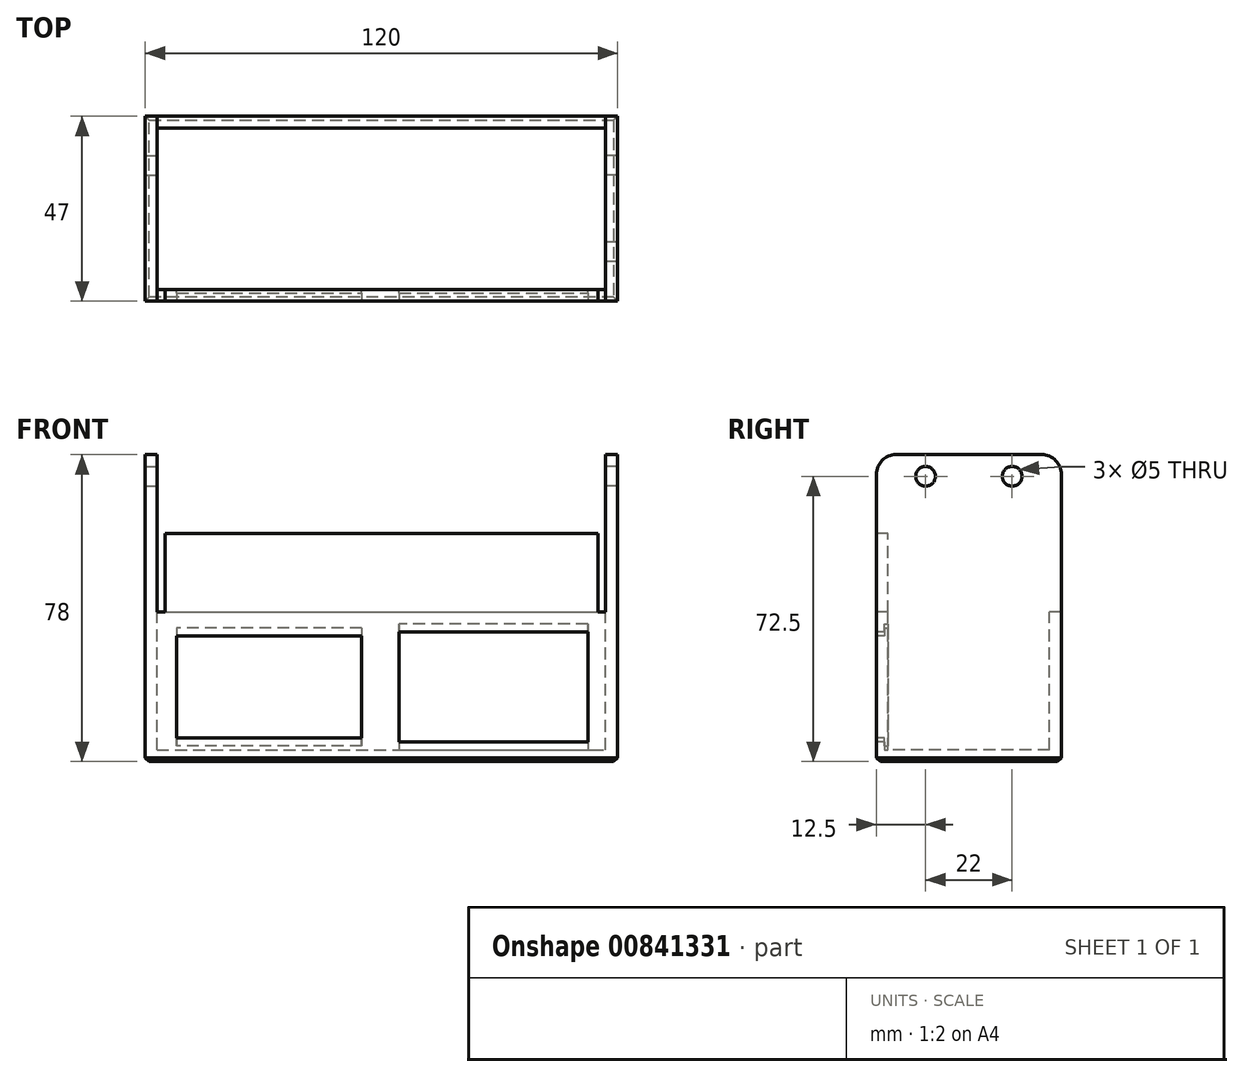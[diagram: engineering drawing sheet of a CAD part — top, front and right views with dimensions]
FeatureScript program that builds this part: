
annotation { "Feature Type Name" : "Feature", "Feature Type Description" : "" }
export const myFeature = defineFeature(function(context is Context, id is Id, definition is map)
    precondition{}
    {
        {
            assignVariable(context, id + "F0", {"name" : "wall", "anyValue" : 3});
        }
        {
            assignVariable(context, id + "F1", {"name" : "width", "anyValue" : 114});
        }
        {
            var Q0;
            Q0=qCreatedBy(makeId("Right.planeOp"),FACE);
            var sketch = newSketch(context, id + "F2", { "sketchPlane" : qUnion([Q0])});
            skLineSegment(sketch, "E0.bottom", {"start": v(17.5, 40) * mm, "end": v(-19.5, 40) * mm});
            skLineSegment(sketch, "E0.top", {"start": v(22.5, -38) * mm, "end": v(-24.5, -38) * mm});
            skLineSegment(sketch, "E0.left", {"start": v(22.5, 35) * mm, "end": v(22.5, -38) * mm});
            skLineSegment(sketch, "E0.right", {"start": v(-24.5, 35) * mm, "end": v(-24.5, -38) * mm});
            skCircle(sketch, "E1", {"center": v(10, 34.5) * mm, "radius": 2.5 * mm});
            skCircle(sketch, "E2", {"center": v(-12, 34.5) * mm, "radius": 2.5 * mm});
            skPoint(sketch, "E3.visualSharp", {"position": v(-24.5, 40) * mm});
            skArc(sketch, "E3.filletArc", {"start": v(-19.5, 40) * mm, "mid": v(-23.04, 38.54) * mm, "end": v(-24.5, 35) * mm});
            skPoint(sketch, "E4.visualSharp", {"position": v(22.5, 40) * mm});
            skArc(sketch, "E4.filletArc", {"start": v(22.5, 35) * mm, "mid": v(21.04, 38.54) * mm, "end": v(17.5, 40) * mm});
            skSolve(sketch);
        }
        {
            var Q0;
            Q0=qSketchRegion(id+"F2",true);
            extrude(context, id + "F3", {"entities" : qUnion([Q0]), "depth" : (getVariable(context, 'wall')) * mm, "offsetDistance" : 25 * mm});
        }
        {
            var Q0;
            Q0=qCreatedBy(makeId("Right.planeOp"),FACE);
            var sketch = newSketch(context, id + "F4", { "sketchPlane" : qUnion([Q0])});
            skLineSegment(sketch, "E5.bottom", {"start": v(22.5, -38) * mm, "end": v(-24.5, -38) * mm});
            skLineSegment(sketch, "E5.top", {"start": v(22.5, -35) * mm, "end": v(-24.5, -35) * mm});
            skLineSegment(sketch, "E5.left", {"start": v(22.5, -38) * mm, "end": v(22.5, -35) * mm});
            skLineSegment(sketch, "E5.right", {"start": v(-24.5, -38) * mm, "end": v(-24.5, -35) * mm});
            skLineSegment(sketch, "E6.bottom", {"start": v(-24.5, -38) * mm, "end": v(-21.5, -38) * mm});
            skLineSegment(sketch, "E6.top", {"start": v(-24.5, 0) * mm, "end": v(-21.5, 0) * mm});
            skLineSegment(sketch, "E6.left", {"start": v(-24.5, -38) * mm, "end": v(-24.5, 0) * mm});
            skLineSegment(sketch, "E6.right", {"start": v(-21.5, -38) * mm, "end": v(-21.5, 0) * mm});
            skLineSegment(sketch, "E7.bottom", {"start": v(22.5, -38) * mm, "end": v(19.5, -38) * mm});
            skLineSegment(sketch, "E7.top", {"start": v(22.5, 0) * mm, "end": v(19.5, 0) * mm});
            skLineSegment(sketch, "E7.left", {"start": v(22.5, -38) * mm, "end": v(22.5, 0) * mm});
            skLineSegment(sketch, "E7.right", {"start": v(19.5, -38) * mm, "end": v(19.5, 0) * mm});
            skSolve(sketch);
        }
        {
            var Q0;
            {var subQ0=sQuery(id+"F4.wireOp",EDGE,"E5.right");var subQ1=sQuery(id+"F4.wireOp",EDGE,"E5.bottom");var subQ9=sQuery(id+"F4.wireOp",EDGE,"E7.right");var subQ10=makeQuery(id+"F4.imprint","INTERSECT",VERTEX,{"derivedFrom":[subQ1,subQ9]});var subQ14=sQuery(id+"F4.wireOp",EDGE,"E5.left");var subQ16=sQuery(id+"F4.wireOp",EDGE,"E7.top");var subQ17=sQuery(id+"F4.wireOp",EDGE,"E6.top");Q0=qUnion([makeQuery(id+"F4.imprint","IMPRINT",FACE,{"disambiguationData":[TD([[makeQuery(id+"F4.imprint","IMPRINT",EDGE,{"derivedFrom":subQ17}),-1.0]])]}),makeQuery(id+"F4.imprint","IMPRINT",FACE,{"disambiguationData":[TD([[makeQuery(id+"F4.imprint","IMPRINT",EDGE,{"derivedFrom":subQ14}),1.0]])]}),makeQuery(id+"F4.imprint","IMPRINT",FACE,{"disambiguationData":[TD([[makeQuery(id+"F4.imprint","IMPRINT",EDGE,{"derivedFrom":subQ16}),1.0]])]}),makeQuery(id+"F4.imprint","IMPRINT",FACE,{"disambiguationData":[TD([[makeQuery(id+"F4.imprint","IMPRINT",EDGE,{"disambiguationData":[TD([[subQ10,-1.0]])],"derivedFrom":subQ1}),-1.0]])]}),makeQuery(id+"F4.imprint","IMPRINT",FACE,{"disambiguationData":[TD([[makeQuery(id+"F4.imprint","IMPRINT",EDGE,{"derivedFrom":subQ0}),-1.0]])]})]);}
            extrude(context, id + "F5", {"entities" : qUnion([Q0]), "operationType" : NewBodyOperationType.ADD, "oppositeDirection" : true, "depth" : (getVariable(context, 'width')) * mm, "offsetDistance" : 25 * mm});
        }
        {
            var Q0;
            Q0=makeQuery(id+"F5.opExtrude","CAP_FACE",FACE,{"disambiguationData":[OSD([sQuery(id+"F4.wireOp",EDGE,"E5.bottom"),sQuery(id+"F4.wireOp",EDGE,"E5.top"),sQuery(id+"F4.wireOp",EDGE,"E5.left"),sQuery(id+"F4.wireOp",EDGE,"E5.right"),sQuery(id+"F4.wireOp",EDGE,"E6.top"),sQuery(id+"F4.wireOp",EDGE,"E6.left"),sQuery(id+"F4.wireOp",EDGE,"E6.right"),sQuery(id+"F4.wireOp",EDGE,"E7.top"),sQuery(id+"F4.wireOp",EDGE,"E7.left"),sQuery(id+"F4.wireOp",EDGE,"E7.right")])],"isStart":false});
            var sketch = newSketch(context, id + "F6", { "sketchPlane" : qUnion([Q0])});
            skLineSegment(sketch, "E8.bottom", {"start": v(19.5, 40) * mm, "end": v(-17.5, 40) * mm});
            skLineSegment(sketch, "E8.top", {"start": v(24.5, -38) * mm, "end": v(-22.5, -38) * mm});
            skLineSegment(sketch, "E8.left", {"start": v(24.5, 35) * mm, "end": v(24.5, -38) * mm});
            skLineSegment(sketch, "E8.right", {"start": v(-22.5, 35) * mm, "end": v(-22.5, -38) * mm});
            skCircle(sketch, "E9", {"center": v(-10, 34.5) * mm, "radius": 2.5 * mm});
            skPoint(sketch, "E10.visualSharp", {"position": v(-22.5, 40) * mm});
            skArc(sketch, "E10.filletArc", {"start": v(-17.5, 40) * mm, "mid": v(-21.04, 38.54) * mm, "end": v(-22.5, 35) * mm});
            skPoint(sketch, "E11.visualSharp", {"position": v(24.5, 40) * mm});
            skArc(sketch, "E11.filletArc", {"start": v(24.5, 35) * mm, "mid": v(23.04, 38.54) * mm, "end": v(19.5, 40) * mm});
            skSolve(sketch);
        }
        {
            var Q0;
            Q0=qSketchRegion(id+"F6",true);
            extrude(context, id + "F7", {"entities" : qUnion([Q0]), "operationType" : NewBodyOperationType.ADD, "depth" : (getVariable(context, 'wall')) * mm, "offsetDistance" : 25 * mm});
        }
        {
            var Q0;
            Q0=makeQuery(id+"F7.boolean.opBoolean","MERGE",FACE,{"derivedFrom":[makeQuery(id+"F5.boolean.opBoolean","MERGE",FACE,{"derivedFrom":[makeQuery(id+"F3.opExtrude","SWEPT_FACE",FACE,{"disambiguationData":[OSD([sQuery(id+"F2.wireOp",EDGE,"E0.right")])]}),makeQuery(id+"F5.opExtrude","SWEPT_FACE",FACE,{"disambiguationData":[OSD([sQuery(id+"F4.wireOp",EDGE,"E5.right"),sQuery(id+"F4.wireOp",EDGE,"E6.left")])]})]}),makeQuery(id+"F7.opExtrude","SWEPT_FACE",FACE,{"disambiguationData":[OSD([sQuery(id+"F6.wireOp",EDGE,"E8.left")])]})]});
            var sketch = newSketch(context, id + "F8", { "sketchPlane" : qUnion([Q0])});
            skLineSegment(sketch, "E12.bottom", {"start": v(-112, 0) * mm, "end": v(-2, 0) * mm});
            skLineSegment(sketch, "E12.top", {"start": v(-112, 20) * mm, "end": v(-2, 20) * mm});
            skLineSegment(sketch, "E12.left", {"start": v(-112, 0) * mm, "end": v(-112, 20) * mm});
            skLineSegment(sketch, "E12.right", {"start": v(-2, 0) * mm, "end": v(-2, 20) * mm});
            skSolve(sketch);
        }
        {
            var Q0;
            Q0=qSketchRegion(id+"F8",true);
            extrude(context, id + "F9", {"entities" : qUnion([Q0]), "operationType" : NewBodyOperationType.ADD, "oppositeDirection" : true, "depth" : (getVariable(context, 'wall')) * mm, "offsetDistance" : 25 * mm});
        }
        {
            var Q0;
            {var subQ2=sQuery(id+"F8.wireOp",EDGE,"E12.bottom");Q0=makeQuery(id+"F8.imprint","IMPRINT",FACE,{"disambiguationData":[TD([[makeQuery(id+"F8.imprint","IMPRINT",EDGE,{"derivedFrom":subQ2}),-1.0]])]});}
            var sketch = newSketch(context, id + "F10", { "sketchPlane" : qUnion([Q0])});
            skLineSegment(sketch, "E13.bottom", {"start": v(-109, -6) * mm, "end": v(-62, -6) * mm});
            skLineSegment(sketch, "E13.top", {"start": v(-109, -32) * mm, "end": v(-62, -32) * mm});
            skLineSegment(sketch, "E13.left", {"start": v(-109, -6) * mm, "end": v(-109, -32) * mm});
            skLineSegment(sketch, "E13.right", {"start": v(-62, -6) * mm, "end": v(-62, -32) * mm});
            skLineSegment(sketch, "E14.bottom", {"start": v(-52.5, -5) * mm, "end": v(-4.5, -5) * mm});
            skLineSegment(sketch, "E14.top", {"start": v(-52.5, -33) * mm, "end": v(-4.5, -33) * mm});
            skLineSegment(sketch, "E14.left", {"start": v(-52.5, -5) * mm, "end": v(-52.5, -33) * mm});
            skLineSegment(sketch, "E14.right", {"start": v(-4.5, -5) * mm, "end": v(-4.5, -33) * mm});
            skLineSegment(sketch, "E15", {"start": v(-57, 0) * mm, "end": v(-57, -48.8) * mm, "construction": true});
            skLineSegment(sketch, "E16", {"start": v(-121.46, -19) * mm, "end": v(11.47, -19) * mm, "construction": true});
            skSolve(sketch);
        }
        {
            var Q0;
            Q0=qSketchRegion(id+"F10",true);
            extrude(context, id + "F11", {"entities" : qUnion([Q0]), "operationType" : NewBodyOperationType.REMOVE, "endBound" : BoundingType.UP_TO_NEXT, "oppositeDirection" : true, "depth" : 25 * mm, "offsetDistance" : 25 * mm});
        }
        {
            var Q0;
            Q0=makeQuery(id+"F7.boolean.opBoolean","MERGE",FACE,{"derivedFrom":[makeQuery(id+"F5.boolean.opBoolean","MERGE",FACE,{"derivedFrom":[makeQuery(id+"F3.opExtrude","SWEPT_FACE",FACE,{"disambiguationData":[OSD([sQuery(id+"F2.wireOp",EDGE,"E0.top")])]}),makeQuery(id+"F5.opExtrude","SWEPT_FACE",FACE,{"disambiguationData":[OSD([sQuery(id+"F4.wireOp",EDGE,"E5.bottom")])]})]}),makeQuery(id+"F7.opExtrude","SWEPT_FACE",FACE,{"disambiguationData":[OSD([sQuery(id+"F6.wireOp",EDGE,"E8.top")])]})]});
            chamfer(context, id + "F12", {"entities" : qUnion([Q0]), "width" : 1 * mm, "tangentPropagation" : true});
        }
        {
            assignVariable(context, id + "F13", {"name" : "InsertClipD", "anyValue" : 1});
        }
        {
            var Q0;
            Q0=makeQuery(id+"F9.boolean.opBoolean","MERGE",FACE,{"derivedFrom":[makeQuery(id+"F5.opExtrude","SWEPT_FACE",FACE,{"disambiguationData":[OSD([sQuery(id+"F4.wireOp",EDGE,"E6.right")])]}),makeQuery(id+"F9.opExtrude","CAP_FACE",FACE,{"disambiguationData":[OSD([sQuery(id+"F8.wireOp",EDGE,"E12.bottom"),sQuery(id+"F8.wireOp",EDGE,"E12.top"),sQuery(id+"F8.wireOp",EDGE,"E12.left"),sQuery(id+"F8.wireOp",EDGE,"E12.right")])],"isStart":false})]});
            var sketch = newSketch(context, id + "F14", { "sketchPlane" : qUnion([Q0])});
            skLineSegment(sketch, "E17.bottom", {"start": v(4.5, -5) * mm, "end": v(52.5, -5) * mm});
            skLineSegment(sketch, "E17.top", {"start": v(4.5, -3) * mm, "end": v(52.5, -3) * mm});
            skLineSegment(sketch, "E17.left", {"start": v(4.5, -5) * mm, "end": v(4.5, -3) * mm});
            skLineSegment(sketch, "E17.right", {"start": v(52.5, -5) * mm, "end": v(52.5, -3) * mm});
            skLineSegment(sketch, "E18.bottom", {"start": v(4.5, -33) * mm, "end": v(52.5, -33) * mm});
            skLineSegment(sketch, "E18.top", {"start": v(4.5, -35) * mm, "end": v(52.5, -35) * mm});
            skLineSegment(sketch, "E18.left", {"start": v(4.5, -33) * mm, "end": v(4.5, -35) * mm});
            skLineSegment(sketch, "E18.right", {"start": v(52.5, -33) * mm, "end": v(52.5, -35) * mm});
            skLineSegment(sketch, "E19.bottom", {"start": v(62, -4) * mm, "end": v(109, -4) * mm});
            skLineSegment(sketch, "E19.top", {"start": v(62, -6) * mm, "end": v(109, -6) * mm});
            skLineSegment(sketch, "E19.left", {"start": v(62, -4) * mm, "end": v(62, -6) * mm});
            skLineSegment(sketch, "E19.right", {"start": v(109, -4) * mm, "end": v(109, -6) * mm});
            skLineSegment(sketch, "E20.bottom", {"start": v(62, -34) * mm, "end": v(109, -34) * mm});
            skLineSegment(sketch, "E20.top", {"start": v(62, -32) * mm, "end": v(109, -32) * mm});
            skLineSegment(sketch, "E20.left", {"start": v(62, -34) * mm, "end": v(62, -32) * mm});
            skLineSegment(sketch, "E20.right", {"start": v(109, -34) * mm, "end": v(109, -32) * mm});
            skSolve(sketch);
        }
        {
            var Q0;
            Q0=makeQuery(id+"F14.imprint","IMPRINT",FACE,{"disambiguationData":[TD([[makeQuery(id+"F14.imprint","IMPRINT",EDGE,{"derivedFrom":sQuery(id+"F14.wireOp",EDGE,"E18.bottom")}),1.0]])]});
            var Q1;
            Q1=makeQuery(id+"F14.imprint","IMPRINT",FACE,{"disambiguationData":[TD([[makeQuery(id+"F14.imprint","IMPRINT",EDGE,{"derivedFrom":sQuery(id+"F14.wireOp",EDGE,"E20.bottom")}),1.0]])]});
            var Q2;
            Q2=makeQuery(id+"F14.imprint","IMPRINT",FACE,{"disambiguationData":[TD([[makeQuery(id+"F14.imprint","IMPRINT",EDGE,{"derivedFrom":sQuery(id+"F14.wireOp",EDGE,"E19.bottom")}),-1.0]])]});
            var Q3;
            Q3=makeQuery(id+"F14.imprint","IMPRINT",FACE,{"disambiguationData":[TD([[makeQuery(id+"F14.imprint","IMPRINT",EDGE,{"derivedFrom":sQuery(id+"F14.wireOp",EDGE,"E17.bottom")}),-1.0]])]});
            extrude(context, id + "F15", {"entities" : qUnion([Q0, Q1, Q2, Q3]), "operationType" : NewBodyOperationType.REMOVE, "oppositeDirection" : true, "depth" : (getVariable(context, 'InsertClipD')) * mm, "offsetDistance" : 25 * mm});
        }
    });
